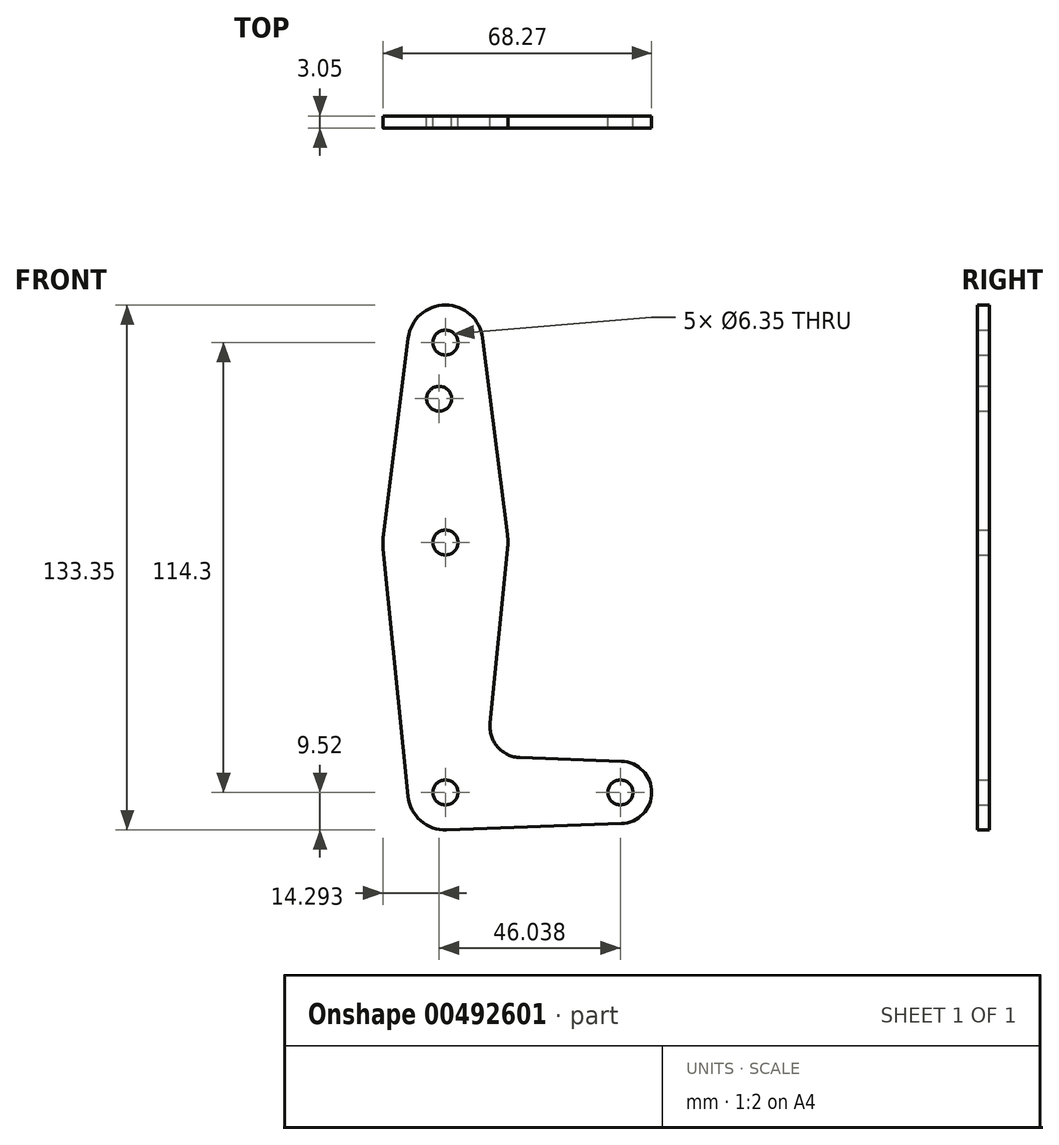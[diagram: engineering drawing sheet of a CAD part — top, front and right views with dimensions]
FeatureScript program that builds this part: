
annotation { "Feature Type Name" : "Feature", "Feature Type Description" : "" }
export const myFeature = defineFeature(function(context is Context, id is Id, definition is map)
    precondition{}
    {
        {
            var Q0;
            Q0=qCreatedBy(makeId("Front.planeOp"),FACE);
            var sketch = newSketch(context, id + "F0", { "sketchPlane" : qUnion([Q0])});
            skLineSegment(sketch, "E0", {"start": v(0, 114.3) * mm, "end": v(0, 0) * mm, "construction": true});
            skLineSegment(sketch, "E1", {"start": v(0, 0) * mm, "end": v(44.45, 0) * mm, "construction": true});
            skCircle(sketch, "E2", {"center": v(0, 114.3) * mm, "radius": 9.53 * mm});
            skCircle(sketch, "E3", {"center": v(44.45, 0) * mm, "radius": 7.94 * mm});
            skCircle(sketch, "E4", {"center": v(0, 63.5) * mm, "radius": 15.88 * mm});
            skCircle(sketch, "E5", {"center": v(0, 114.3) * mm, "radius": 3.18 * mm});
            skCircle(sketch, "E6", {"center": v(-1.59, 100.03) * mm, "radius": 3.18 * mm});
            skCircle(sketch, "E7", {"center": v(0, 63.5) * mm, "radius": 3.18 * mm});
            skCircle(sketch, "E8", {"center": v(0, 0) * mm, "radius": 3.18 * mm});
            skCircle(sketch, "E9", {"center": v(44.45, 0) * mm, "radius": 3.18 * mm});
            skCircle(sketch, "E10", {"center": v(0, 0) * mm, "radius": 9.53 * mm});
            skLineSegment(sketch, "E11", {"start": v(-9.45, 115.5) * mm, "end": v(-15.75, 65.48) * mm});
            skLineSegment(sketch, "E12", {"start": v(9.45, 115.5) * mm, "end": v(15.75, 65.48) * mm});
            skLineSegment(sketch, "E13", {"start": v(-15.8, 61.91) * mm, "end": v(-9.48, -0.95) * mm});
            skLineSegment(sketch, "E14", {"start": v(15.8, 61.91) * mm, "end": v(11.34, 17.6) * mm});
            skLineSegment(sketch, "E15", {"start": v(44.73, 7.93) * mm, "end": v(18.97, 8.85) * mm});
            skLineSegment(sketch, "E16", {"start": v(0.34, -9.52) * mm, "end": v(44.73, -7.93) * mm});
            skPoint(sketch, "E17.newPointB", {"position": v(0, 9.53) * mm});
            skArc(sketch, "E17.filletArc", {"start": v(11.34, 17.6) * mm, "mid": v(13.26, 11.57) * mm, "end": v(18.97, 8.85) * mm});
            skSolve(sketch);
        }
        {
            var Q0;
            Q0 = qSketchRegion(id + "F0", true);
            extrude(context, id + "F1", {"entities" : qUnion([Q0]), "depth" : 3.05 * mm});
        }
    });
